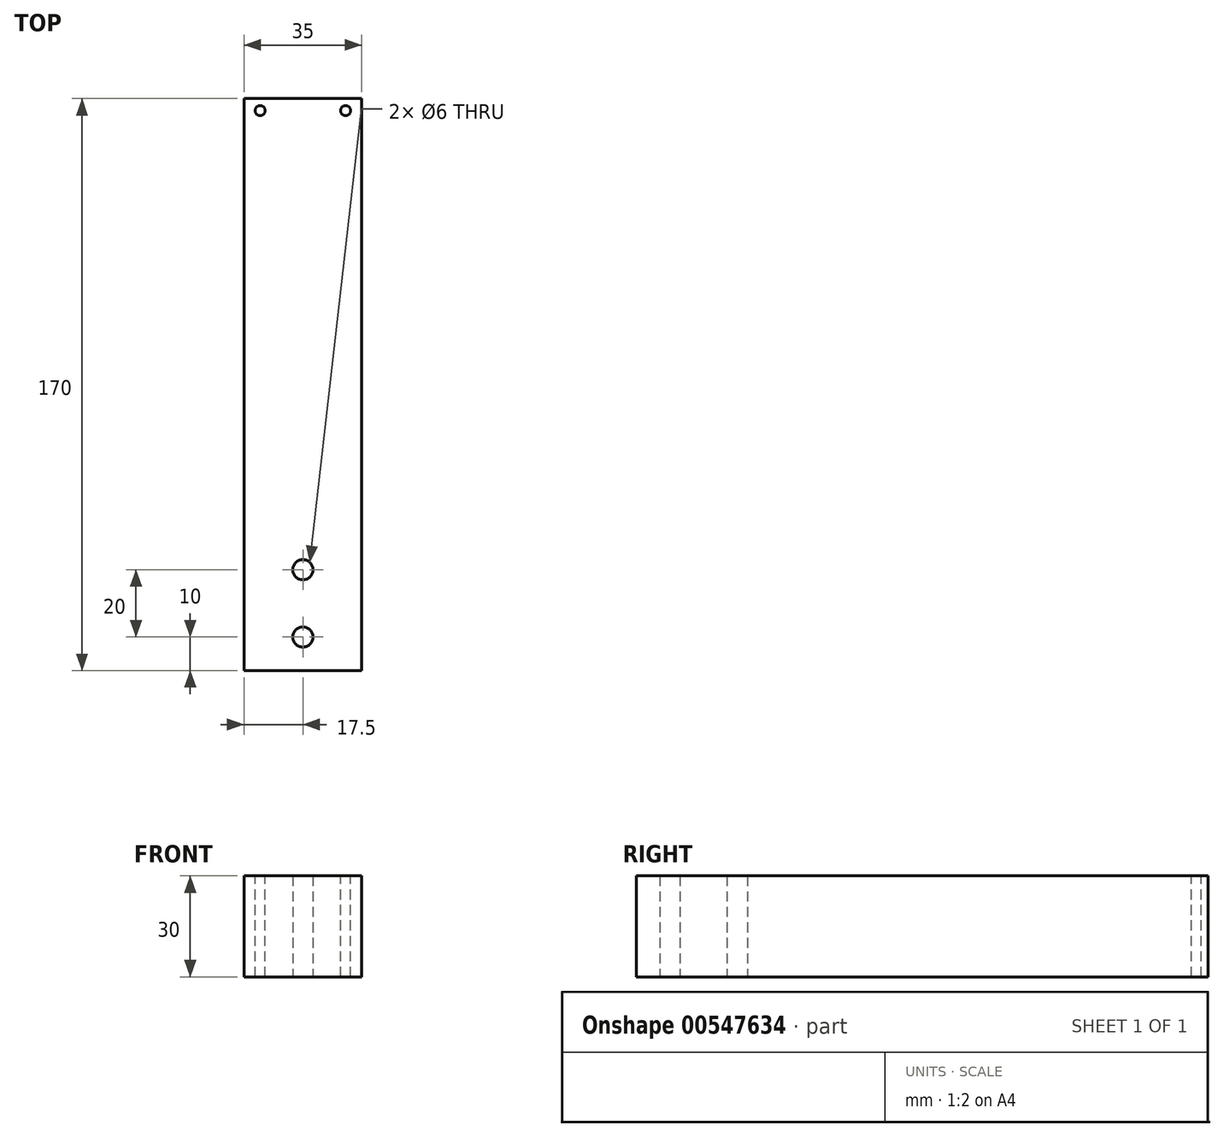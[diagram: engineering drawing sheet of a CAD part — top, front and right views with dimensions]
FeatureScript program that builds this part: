
annotation { "Feature Type Name" : "Feature", "Feature Type Description" : "" }
export const myFeature = defineFeature(function(context is Context, id is Id, definition is map)
    precondition{}
    {
        {
            var Q0;
            Q0=qCreatedBy(makeId("Top.planeOp"),FACE);
            var sketch = newSketch(context, id + "F0", { "sketchPlane" : qUnion([Q0])});
            skLineSegment(sketch, "E0.bottom", {"start": v(17.5, 85) * mm, "end": v(-17.5, 85) * mm});
            skLineSegment(sketch, "E0.top", {"start": v(17.5, -85) * mm, "end": v(-17.5, -85) * mm});
            skLineSegment(sketch, "E0.left", {"start": v(17.5, 85) * mm, "end": v(17.5, -85) * mm});
            skLineSegment(sketch, "E0.right", {"start": v(-17.5, 85) * mm, "end": v(-17.5, -85) * mm});
            skPoint(sketch, "E0.middle", {"position": v(0, 0) * mm});
            skCircle(sketch, "E1", {"center": v(0, -55) * mm, "radius": 3 * mm});
            skCircle(sketch, "E2", {"center": v(0, -75) * mm, "radius": 3 * mm});
            skSolve(sketch);
        }
        {
            var Q0;
            Q0=makeQuery(id+"F0.imprint","IMPRINT",FACE,{"disambiguationData":[TD([[makeQuery(id+"F0.imprint","IMPRINT",EDGE,{"derivedFrom":sQuery(id+"F0.wireOp",EDGE,"E0.bottom")}),1.0]])]});
            extrude(context, id + "F1", {"entities" : qUnion([Q0]), "depth" : 30 * mm, "offsetDistance" : 25 * mm});
        }
        {
            var Q0;
            Q0=makeQuery(id+"F1.opExtrude","CAP_FACE",FACE,{"disambiguationData":[OSD([sQuery(id+"F0.wireOp",EDGE,"E0.bottom"),sQuery(id+"F0.wireOp",EDGE,"E0.top"),sQuery(id+"F0.wireOp",EDGE,"E0.left"),sQuery(id+"F0.wireOp",EDGE,"E0.right"),sQuery(id+"F0.wireOp",EDGE,"E1"),sQuery(id+"F0.wireOp",EDGE,"E2")])],"isStart":false});
            var sketch = newSketch(context, id + "F2", { "sketchPlane" : qUnion([Q0])});
            skCircle(sketch, "E3", {"center": v(-12.7, 81.46) * mm, "radius": 1.5 * mm});
            skCircle(sketch, "E4", {"center": v(12.7, 81.46) * mm, "radius": 1.5 * mm});
            skLineSegment(sketch, "E5", {"start": v(-12.7, 81.46) * mm, "end": v(12.7, 81.46) * mm, "construction": true});
            skPoint(sketch, "E6", {"position": v(0, 81.46) * mm});
            skSolve(sketch);
        }
        {
            var Q0;
            Q0 = qSketchRegion(id + "F2", true);
            extrude(context, id + "F3", {"entities" : qUnion([Q0]), "operationType" : NewBodyOperationType.REMOVE, "endBound" : BoundingType.THROUGH_ALL, "oppositeDirection" : true, "depth" : 25 * mm, "offsetDistance" : 25 * mm});
        }
    });
